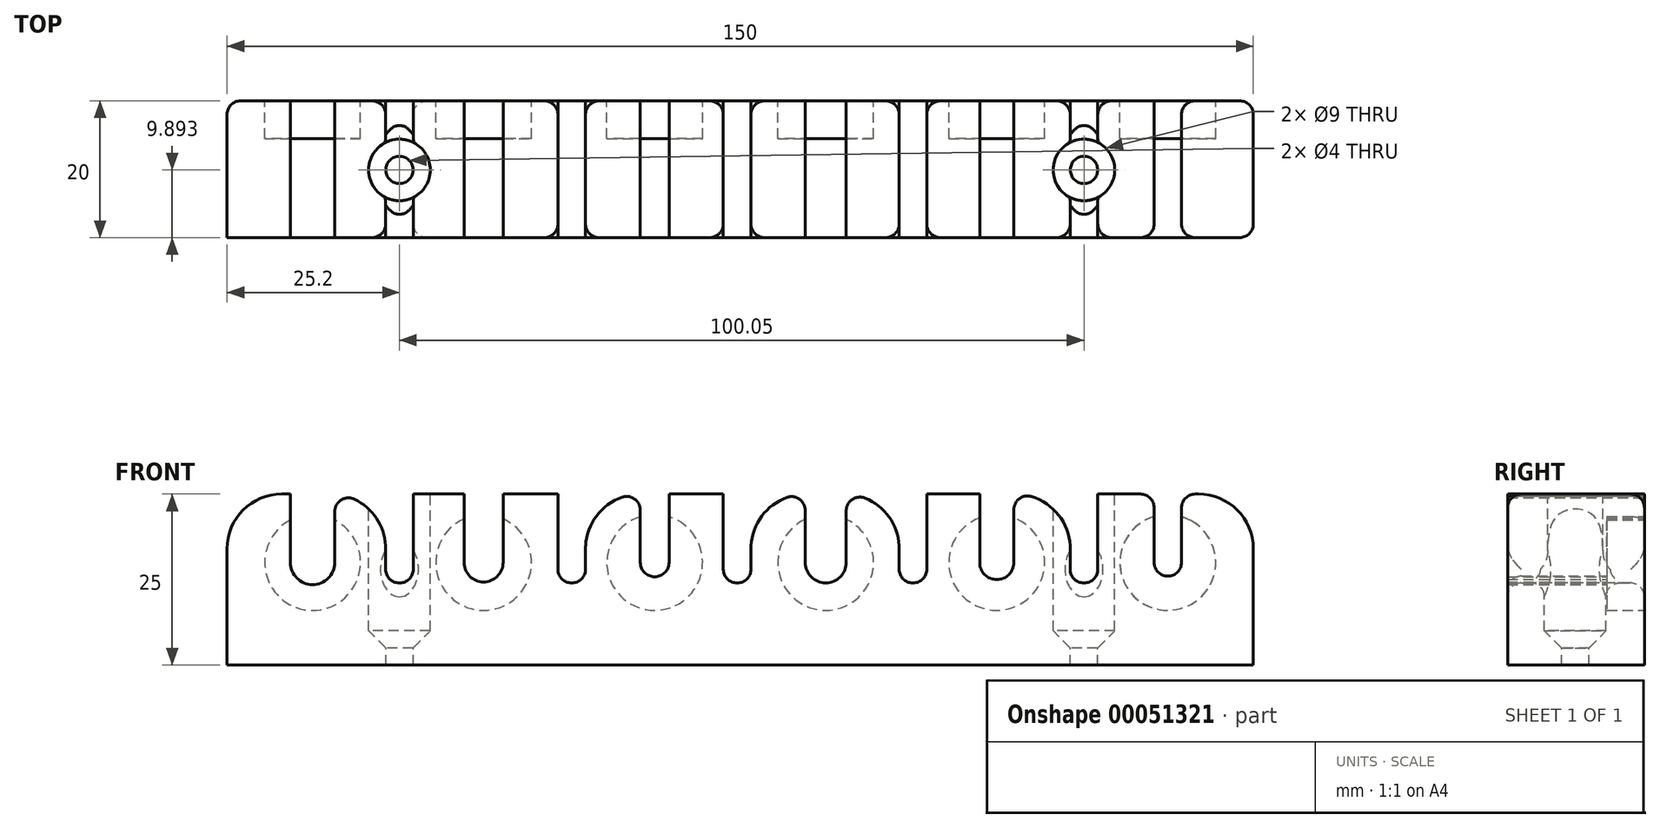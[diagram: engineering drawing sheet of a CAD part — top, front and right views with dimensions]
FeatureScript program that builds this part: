
annotation { "Feature Type Name" : "Feature", "Feature Type Description" : "" }
export const myFeature = defineFeature(function(context is Context, id is Id, definition is map)
    precondition{}
    {
        {
            var Q0;
            Q0=qCreatedBy(makeId("Top.planeOp"),FACE);
            var sketch = newSketch(context, id + "F0", { "sketchPlane" : qUnion([Q0])});
            skLineSegment(sketch, "E0.bottom", {"start": v(0, 0) * mm, "end": v(150, 0) * mm});
            skLineSegment(sketch, "E0.top", {"start": v(0, 20) * mm, "end": v(150, 20) * mm});
            skLineSegment(sketch, "E0.left", {"start": v(0, 0) * mm, "end": v(0, 20) * mm});
            skLineSegment(sketch, "E0.right", {"start": v(150, 0) * mm, "end": v(150, 20) * mm});
            skSolve(sketch);
        }
        {
            var Q0;
            Q0 = qSketchRegion(id + "F0", true);
            extrude(context, id + "F1", {"entities" : qUnion([Q0]), "depth" : 25 * mm});
        }
        {
            var Q0;
            Q0=makeQuery(id+"F1.opExtrude","SWEPT_FACE",FACE,{"disambiguationData":[OSD([sQuery(id+"F0.wireOp",EDGE,"E0.top")])]});
            var sketch = newSketch(context, id + "F2", { "sketchPlane" : qUnion([Q0])});
            skLineSegment(sketch, "E1", {"start": v(0, 15) * mm, "end": v(-150, 15) * mm, "construction": true});
            skLineSegment(sketch, "E2", {"start": v(-75, 0) * mm, "end": v(-75, 25) * mm, "construction": true});
            skCircle(sketch, "E3", {"center": v(-62.5, 15) * mm, "radius": 7 * mm});
            skCircle(sketch, "E4", {"center": v(-37.5, 15) * mm, "radius": 7 * mm});
            skCircle(sketch, "E5", {"center": v(-12.5, 15) * mm, "radius": 7 * mm});
            skCircle(sketch, "E6.MirrorC", {"center": v(-87.5, 15) * mm, "radius": 7 * mm});
            skCircle(sketch, "E7.MirrorC", {"center": v(-112.5, 15) * mm, "radius": 7 * mm});
            skCircle(sketch, "E8.MirrorC", {"center": v(-137.5, 15) * mm, "radius": 7 * mm});
            skSolve(sketch);
        }
        {
            var Q0;
            Q0 = qSketchRegion(id + "F2", true);
            extrude(context, id + "F3", {"entities" : qUnion([Q0]), "operationType" : NewBodyOperationType.REMOVE, "oppositeDirection" : true, "depth" : 5.5 * mm});
        }
        {
            var Q0;
            Q0=makeQuery(id+"F1.opExtrude","SWEPT_FACE",FACE,{"disambiguationData":[OSD([sQuery(id+"F0.wireOp",EDGE,"E0.top")])]});
            var sketch = newSketch(context, id + "F4", { "sketchPlane" : qUnion([Q0])});
            skCircle(sketch, "E9", {"center": v(-12.5, 15) * mm, "radius": 3.25 * mm});
            skCircle(sketch, "E10", {"center": v(-37.5, 15) * mm, "radius": 2.85 * mm});
            skCircle(sketch, "E11", {"center": v(-62.5, 15) * mm, "radius": 2.1 * mm});
            skCircle(sketch, "E12", {"center": v(-87.5, 15) * mm, "radius": 3 * mm});
            skCircle(sketch, "E13", {"center": v(-112.5, 15) * mm, "radius": 2.5 * mm});
            skCircle(sketch, "E14", {"center": v(-137.5, 15) * mm, "radius": 2 * mm});
            skSolve(sketch);
        }
        {
            var Q0;
            Q0 = qSketchRegion(id + "F4", true);
            extrude(context, id + "F5", {"entities" : qUnion([Q0]), "operationType" : NewBodyOperationType.REMOVE, "endBound" : BoundingType.THROUGH_ALL, "oppositeDirection" : true, "depth" : 25 * mm});
        }
        {
            var Q0;
            Q0=makeQuery(id+"F1.opExtrude","CAP_FACE",FACE,{"disambiguationData":[OSD([sQuery(id+"F0.wireOp",EDGE,"E0.bottom"),sQuery(id+"F0.wireOp",EDGE,"E0.top"),sQuery(id+"F0.wireOp",EDGE,"E0.left"),sQuery(id+"F0.wireOp",EDGE,"E0.right")])],"isStart":false});
            var sketch = newSketch(context, id + "F6", { "sketchPlane" : qUnion([Q0])});
            skLineSegment(sketch, "E15.0", {"start": v(135.5, 14.5) * mm, "end": v(139.5, 14.5) * mm});
            skLineSegment(sketch, "E16.0", {"start": v(110, 14.5) * mm, "end": v(115, 14.5) * mm});
            skLineSegment(sketch, "E17.0", {"start": v(84.5, 14.5) * mm, "end": v(90.5, 14.5) * mm});
            skLineSegment(sketch, "E18.0", {"start": v(60.4, 14.5) * mm, "end": v(64.6, 14.5) * mm});
            skLineSegment(sketch, "E19.0", {"start": v(34.65, 14.5) * mm, "end": v(40.35, 14.5) * mm});
            skLineSegment(sketch, "E20.0", {"start": v(9.25, 14.5) * mm, "end": v(15.75, 14.5) * mm});
            skLineSegment(sketch, "E21", {"start": v(9.25, 20) * mm, "end": v(9.25, 0) * mm});
            skLineSegment(sketch, "E22", {"start": v(9.25, 0) * mm, "end": v(15.75, 0) * mm});
            skLineSegment(sketch, "E23", {"start": v(15.75, 0) * mm, "end": v(15.75, 20) * mm});
            skLineSegment(sketch, "E24", {"start": v(15.75, 20) * mm, "end": v(9.25, 20) * mm});
            skLineSegment(sketch, "E25", {"start": v(34.65, 14.5) * mm, "end": v(34.65, 20) * mm});
            skLineSegment(sketch, "E26", {"start": v(34.65, 20) * mm, "end": v(40.35, 20) * mm});
            skLineSegment(sketch, "E27", {"start": v(40.35, 20) * mm, "end": v(40.35, 0) * mm});
            skLineSegment(sketch, "E28", {"start": v(40.35, 0) * mm, "end": v(34.65, 0) * mm});
            skLineSegment(sketch, "E29", {"start": v(34.65, 0) * mm, "end": v(34.65, 14.5) * mm});
            skLineSegment(sketch, "E30", {"start": v(60.4, 14.5) * mm, "end": v(60.4, 20) * mm});
            skLineSegment(sketch, "E31", {"start": v(60.4, 20) * mm, "end": v(64.6, 20) * mm});
            skLineSegment(sketch, "E32", {"start": v(64.6, 20) * mm, "end": v(64.6, 0) * mm});
            skLineSegment(sketch, "E33", {"start": v(64.6, 0) * mm, "end": v(60.4, 0) * mm});
            skLineSegment(sketch, "E34", {"start": v(60.4, 0) * mm, "end": v(60.4, 14.5) * mm});
            skLineSegment(sketch, "E35", {"start": v(84.5, 14.5) * mm, "end": v(84.5, 20) * mm});
            skLineSegment(sketch, "E36", {"start": v(84.5, 20) * mm, "end": v(90.5, 20) * mm});
            skLineSegment(sketch, "E37", {"start": v(90.5, 20) * mm, "end": v(90.5, 0) * mm});
            skLineSegment(sketch, "E38", {"start": v(90.5, 0) * mm, "end": v(84.5, 0) * mm});
            skLineSegment(sketch, "E39", {"start": v(84.5, 0) * mm, "end": v(84.5, 14.5) * mm});
            skLineSegment(sketch, "E40", {"start": v(110, 14.5) * mm, "end": v(110, 20) * mm});
            skLineSegment(sketch, "E41", {"start": v(110, 20) * mm, "end": v(115, 20) * mm});
            skLineSegment(sketch, "E42", {"start": v(115, 20) * mm, "end": v(115, 0) * mm});
            skLineSegment(sketch, "E43", {"start": v(115, 0) * mm, "end": v(110, 0) * mm});
            skLineSegment(sketch, "E44", {"start": v(110, 0) * mm, "end": v(110, 14.5) * mm});
            skLineSegment(sketch, "E45.bottom", {"start": v(135.5, 20) * mm, "end": v(139.5, 20) * mm});
            skLineSegment(sketch, "E45.top", {"start": v(135.5, 0) * mm, "end": v(139.5, 0) * mm});
            skLineSegment(sketch, "E45.left", {"start": v(135.5, 20) * mm, "end": v(135.5, 0) * mm});
            skLineSegment(sketch, "E45.right", {"start": v(139.5, 20) * mm, "end": v(139.5, 0) * mm});
            skSolve(sketch);
        }
        {
            var Q0;
            {var subQ0=sQuery(id+"F6.wireOp",EDGE,"E15.0");Q0=makeQuery(id+"F6.imprint","IMPRINT",FACE,{"disambiguationData":[TD([[makeQuery(id+"F6.imprint","IMPRINT",EDGE,{"derivedFrom":subQ0}),1.0]])]});}
            var Q1;
            {var subQ0=sQuery(id+"F6.wireOp",EDGE,"E15.0");Q1=makeQuery(id+"F6.imprint","IMPRINT",FACE,{"disambiguationData":[TD([[makeQuery(id+"F6.imprint","IMPRINT",EDGE,{"derivedFrom":subQ0}),-1.0]])]});}
            var Q2;
            {var subQ0=sQuery(id+"F6.wireOp",EDGE,"E16.0");Q2=makeQuery(id+"F6.imprint","IMPRINT",FACE,{"disambiguationData":[TD([[makeQuery(id+"F6.imprint","IMPRINT",EDGE,{"derivedFrom":subQ0}),1.0]])]});}
            var Q3;
            {var subQ0=sQuery(id+"F6.wireOp",EDGE,"E16.0");Q3=makeQuery(id+"F6.imprint","IMPRINT",FACE,{"disambiguationData":[TD([[makeQuery(id+"F6.imprint","IMPRINT",EDGE,{"derivedFrom":subQ0}),-1.0]])]});}
            var Q4;
            {var subQ0=sQuery(id+"F6.wireOp",EDGE,"E17.0");Q4=makeQuery(id+"F6.imprint","IMPRINT",FACE,{"disambiguationData":[TD([[makeQuery(id+"F6.imprint","IMPRINT",EDGE,{"derivedFrom":subQ0}),1.0]])]});}
            var Q5;
            {var subQ0=sQuery(id+"F6.wireOp",EDGE,"E17.0");Q5=makeQuery(id+"F6.imprint","IMPRINT",FACE,{"disambiguationData":[TD([[makeQuery(id+"F6.imprint","IMPRINT",EDGE,{"derivedFrom":subQ0}),-1.0]])]});}
            var Q6;
            {var subQ0=sQuery(id+"F6.wireOp",EDGE,"E18.0");Q6=makeQuery(id+"F6.imprint","IMPRINT",FACE,{"disambiguationData":[TD([[makeQuery(id+"F6.imprint","IMPRINT",EDGE,{"derivedFrom":subQ0}),1.0]])]});}
            var Q7;
            {var subQ0=sQuery(id+"F6.wireOp",EDGE,"E18.0");Q7=makeQuery(id+"F6.imprint","IMPRINT",FACE,{"disambiguationData":[TD([[makeQuery(id+"F6.imprint","IMPRINT",EDGE,{"derivedFrom":subQ0}),-1.0]])]});}
            var Q8;
            {var subQ0=sQuery(id+"F6.wireOp",EDGE,"E19.0");Q8=makeQuery(id+"F6.imprint","IMPRINT",FACE,{"disambiguationData":[TD([[makeQuery(id+"F6.imprint","IMPRINT",EDGE,{"derivedFrom":subQ0}),1.0]])]});}
            var Q9;
            {var subQ0=sQuery(id+"F6.wireOp",EDGE,"E19.0");Q9=makeQuery(id+"F6.imprint","IMPRINT",FACE,{"disambiguationData":[TD([[makeQuery(id+"F6.imprint","IMPRINT",EDGE,{"derivedFrom":subQ0}),-1.0]])]});}
            var Q10;
            {var subQ0=sQuery(id+"F6.wireOp",EDGE,"E20.0");Q10=makeQuery(id+"F6.imprint","IMPRINT",FACE,{"disambiguationData":[TD([[makeQuery(id+"F6.imprint","IMPRINT",EDGE,{"derivedFrom":subQ0}),1.0]])]});}
            var Q11;
            {var subQ0=sQuery(id+"F6.wireOp",EDGE,"E20.0");Q11=makeQuery(id+"F6.imprint","IMPRINT",FACE,{"disambiguationData":[TD([[makeQuery(id+"F6.imprint","IMPRINT",EDGE,{"derivedFrom":subQ0}),-1.0]])]});}
            extrude(context, id + "F7", {"entities" : qUnion([Q0, Q1, Q2, Q3, Q4, Q5, Q6, Q7, Q8, Q9, Q10, Q11]), "operationType" : NewBodyOperationType.REMOVE, "oppositeDirection" : true, "depth" : 10 * mm});
        }
        {
            var Q0;
            {var subQ0=sQuery(id+"F0.wireOp",EDGE,"E0.bottom");var subQ1=sQuery(id+"F0.wireOp",EDGE,"E0.top");Q0=makeQuery(id+"F7.boolean.opBoolean","SPLIT",FACE,{"disambiguationData":[TD([makeQuery(id+"F7.opExtrude","SWEPT_FACE",FACE,{"disambiguationData":[OSD([sQuery(id+"F6.wireOp",EDGE,"E42")])]})])],"derivedFrom":makeQuery(id+"F1.opExtrude","CAP_FACE",FACE,{"disambiguationData":[OSD([subQ0,subQ1,sQuery(id+"F0.wireOp",EDGE,"E0.left"),sQuery(id+"F0.wireOp",EDGE,"E0.right")])],"isStart":false})});}
            var sketch = newSketch(context, id + "F8", { "sketchPlane" : qUnion([Q0])});
            skLineSegment(sketch, "E46", {"start": v(0, 9.9) * mm, "end": v(150, 9.9) * mm, "construction": true});
            skCircle(sketch, "E47", {"center": v(25.2, 9.9) * mm, "radius": 2 * mm});
            skCircle(sketch, "E48", {"center": v(125.25, 9.9) * mm, "radius": 2 * mm});
            skLineSegment(sketch, "E49", {"start": v(25.2, 0) * mm, "end": v(25.2, 19.66) * mm, "construction": true});
            skLineSegment(sketch, "E50", {"start": v(125.25, 20) * mm, "end": v(125.25, 0) * mm, "construction": true});
            skSolve(sketch);
        }
        {
            var Q0;
            Q0 = qSketchRegion(id + "F8", true);
            extrude(context, id + "F9", {"entities" : qUnion([Q0]), "operationType" : NewBodyOperationType.REMOVE, "endBound" : BoundingType.THROUGH_ALL, "oppositeDirection" : true, "depth" : 20 * mm});
        }
        {
            var Q0;
            {var subQ0=sQuery(id+"F0.wireOp",EDGE,"E0.bottom");var subQ1=sQuery(id+"F0.wireOp",EDGE,"E0.top");Q0=makeQuery(id+"F7.boolean.opBoolean","SPLIT",FACE,{"disambiguationData":[TD([makeQuery(id+"F7.opExtrude","SWEPT_FACE",FACE,{"disambiguationData":[OSD([sQuery(id+"F6.wireOp",EDGE,"E23")])]})])],"derivedFrom":makeQuery(id+"F1.opExtrude","CAP_FACE",FACE,{"disambiguationData":[OSD([subQ0,subQ1,sQuery(id+"F0.wireOp",EDGE,"E0.left"),sQuery(id+"F0.wireOp",EDGE,"E0.right")])],"isStart":false})});}
            var sketch = newSketch(context, id + "F10", { "sketchPlane" : qUnion([Q0])});
            skCircle(sketch, "E51", {"center": v(25.2, 9.9) * mm, "radius": 4.5 * mm});
            skCircle(sketch, "E52", {"center": v(125.25, 9.9) * mm, "radius": 4.5 * mm});
            skSolve(sketch);
        }
        {
            var Q0;
            Q0 = qSketchRegion(id + "F10", true);
            extrude(context, id + "F11", {"entities" : qUnion([Q0]), "operationType" : NewBodyOperationType.REMOVE, "oppositeDirection" : true, "depth" : 20 * mm});
        }
        {
            var Q0;
            Q0=makeQuery(id+"F11.boolean.opBoolean","INTERSECT",EDGE,{"derivedFrom":[makeQuery(id+"F9.boolean.opBoolean","COPY",FACE,{"derivedFrom":makeQuery(id+"F9.opExtrude","SWEPT_FACE",FACE,{"disambiguationData":[OSD([sQuery(id+"F8.wireOp",EDGE,"E47")])]})}),makeQuery(id+"F11.opExtrude","CAP_FACE",FACE,{"disambiguationData":[OSD([sQuery(id+"F10.wireOp",EDGE,"E51")])],"isStart":false})]});
            var Q1;
            Q1=makeQuery(id+"F11.boolean.opBoolean","INTERSECT",EDGE,{"derivedFrom":[makeQuery(id+"F9.boolean.opBoolean","COPY",FACE,{"derivedFrom":makeQuery(id+"F9.opExtrude","SWEPT_FACE",FACE,{"disambiguationData":[OSD([sQuery(id+"F8.wireOp",EDGE,"E48")])]})}),makeQuery(id+"F11.opExtrude","CAP_FACE",FACE,{"disambiguationData":[OSD([sQuery(id+"F10.wireOp",EDGE,"E52")])],"isStart":false})]});
            chamfer(context, id + "F12", {"entities" : qUnion([Q0, Q1]), "width" : 2.5 * mm, "tangentPropagation" : true});
        }
        {
            var Q0;
            {var subQ0=sQuery(id+"F0.wireOp",EDGE,"E0.bottom");var subQ1=sQuery(id+"F0.wireOp",EDGE,"E0.top");Q0=makeQuery(id+"F7.boolean.opBoolean","SPLIT",FACE,{"disambiguationData":[TD([makeQuery(id+"F7.opExtrude","SWEPT_FACE",FACE,{"disambiguationData":[OSD([sQuery(id+"F6.wireOp",EDGE,"E27")])]})])],"derivedFrom":makeQuery(id+"F1.opExtrude","CAP_FACE",FACE,{"disambiguationData":[OSD([subQ0,subQ1,sQuery(id+"F0.wireOp",EDGE,"E0.left"),sQuery(id+"F0.wireOp",EDGE,"E0.right")])],"isStart":false})});}
            var sketch = newSketch(context, id + "F13", { "sketchPlane" : qUnion([Q0])});
            skLineSegment(sketch, "E53.bottom", {"start": v(48.36, 20) * mm, "end": v(52.4, 20) * mm});
            skLineSegment(sketch, "E53.top", {"start": v(48.36, 0) * mm, "end": v(52.4, 0) * mm});
            skLineSegment(sketch, "E53.left", {"start": v(48.36, 20) * mm, "end": v(48.36, 0) * mm});
            skLineSegment(sketch, "E53.right", {"start": v(52.4, 20) * mm, "end": v(52.4, 0) * mm});
            skLineSegment(sketch, "E54.bottom", {"start": v(72.53, 20) * mm, "end": v(76.57, 20) * mm});
            skLineSegment(sketch, "E54.top", {"start": v(72.53, 0) * mm, "end": v(76.57, 0) * mm});
            skLineSegment(sketch, "E54.left", {"start": v(72.53, 20) * mm, "end": v(72.53, 0) * mm});
            skLineSegment(sketch, "E54.right", {"start": v(76.57, 20) * mm, "end": v(76.57, 0) * mm});
            skLineSegment(sketch, "E55.bottom", {"start": v(98.23, 0) * mm, "end": v(102.27, 0) * mm});
            skLineSegment(sketch, "E55.top", {"start": v(98.23, 20) * mm, "end": v(102.27, 20) * mm});
            skLineSegment(sketch, "E55.left", {"start": v(98.23, 0) * mm, "end": v(98.23, 20) * mm});
            skLineSegment(sketch, "E55.right", {"start": v(102.27, 0) * mm, "end": v(102.27, 20) * mm});
            skLineSegment(sketch, "E56", {"start": v(50.38, 20) * mm, "end": v(50.38, 0) * mm, "construction": true});
            skLineSegment(sketch, "E57", {"start": v(74.55, 20) * mm, "end": v(74.55, 0) * mm, "construction": true});
            skLineSegment(sketch, "E58", {"start": v(100.25, 20) * mm, "end": v(100.25, 0) * mm, "construction": true});
            skLineSegment(sketch, "E59.bottom", {"start": v(23.18, 0) * mm, "end": v(27.22, 0) * mm});
            skLineSegment(sketch, "E59.top", {"start": v(23.18, 20) * mm, "end": v(27.22, 20) * mm});
            skLineSegment(sketch, "E59.left", {"start": v(23.18, 0) * mm, "end": v(23.18, 20) * mm});
            skLineSegment(sketch, "E59.right", {"start": v(27.22, 0) * mm, "end": v(27.22, 20) * mm});
            skLineSegment(sketch, "E60", {"start": v(25.2, 20) * mm, "end": v(25.2, 0) * mm, "construction": true});
            skLineSegment(sketch, "E61.bottom", {"start": v(123.23, 0) * mm, "end": v(127.27, 0) * mm});
            skLineSegment(sketch, "E61.top", {"start": v(123.23, 20) * mm, "end": v(127.27, 20) * mm});
            skLineSegment(sketch, "E61.left", {"start": v(123.23, 0) * mm, "end": v(123.23, 20) * mm});
            skLineSegment(sketch, "E61.right", {"start": v(127.27, 0) * mm, "end": v(127.27, 20) * mm});
            skLineSegment(sketch, "E62", {"start": v(125.25, 20) * mm, "end": v(125.25, 0) * mm, "construction": true});
            skSolve(sketch);
        }
        {
            var Q0;
            Q0 = qSketchRegion(id + "F13", true);
            extrude(context, id + "F14", {"entities" : qUnion([Q0]), "operationType" : NewBodyOperationType.REMOVE, "oppositeDirection" : true, "depth" : 13 * mm});
        }
        {
            var Q0;
            Q0=makeQuery(id+"F14.boolean.opBoolean","COPY",EDGE,{"derivedFrom":makeQuery(id+"F14.opExtrude","CAP_EDGE",EDGE,{"disambiguationData":[OSD([sQuery(id+"F13.wireOp",EDGE,"E53.left")])],"isStart":true})});
            var Q1;
            Q1=makeQuery(id+"F14.boolean.opBoolean","COPY",EDGE,{"derivedFrom":makeQuery(id+"F14.opExtrude","CAP_EDGE",EDGE,{"disambiguationData":[OSD([sQuery(id+"F13.wireOp",EDGE,"E53.right")])],"isStart":true})});
            var Q2;
            Q2=makeQuery(id+"F14.boolean.opBoolean","COPY",EDGE,{"derivedFrom":makeQuery(id+"F14.opExtrude","CAP_EDGE",EDGE,{"disambiguationData":[OSD([sQuery(id+"F13.wireOp",EDGE,"E54.left")])],"isStart":true})});
            var Q3;
            Q3=makeQuery(id+"F14.boolean.opBoolean","COPY",EDGE,{"derivedFrom":makeQuery(id+"F14.opExtrude","CAP_EDGE",EDGE,{"disambiguationData":[OSD([sQuery(id+"F13.wireOp",EDGE,"E54.right")])],"isStart":true})});
            var Q4;
            Q4=makeQuery(id+"F14.boolean.opBoolean","COPY",EDGE,{"derivedFrom":makeQuery(id+"F14.opExtrude","CAP_EDGE",EDGE,{"disambiguationData":[OSD([sQuery(id+"F13.wireOp",EDGE,"E55.left")])],"isStart":true})});
            var Q5;
            Q5=makeQuery(id+"F14.boolean.opBoolean","COPY",EDGE,{"derivedFrom":makeQuery(id+"F14.opExtrude","CAP_EDGE",EDGE,{"disambiguationData":[OSD([sQuery(id+"F13.wireOp",EDGE,"E55.right")])],"isStart":true})});
            var Q6;
            Q6=makeQuery(id+"F1.opExtrude","CAP_EDGE",EDGE,{"disambiguationData":[OSD([sQuery(id+"F0.wireOp",EDGE,"E0.right")])],"isStart":false});
            var Q7;
            Q7=makeQuery(id+"F1.opExtrude","CAP_EDGE",EDGE,{"disambiguationData":[OSD([sQuery(id+"F0.wireOp",EDGE,"E0.left")])],"isStart":false});
            var Q8;
            {var subQ0=sQuery(id+"F0.wireOp",EDGE,"E0.top");var subQ1=sQuery(id+"F0.wireOp",EDGE,"E0.bottom");var subQ3=sQuery(id+"F13.wireOp",EDGE,"E59.left");var subQ6=makeQuery(id+"F14.opExtrude","CAP_EDGE",EDGE,{"disambiguationData":[OSD([subQ3])],"isStart":true});Q8=qUnion([makeQuery(id+"F14.boolean.opBoolean","COPY",EDGE,{"disambiguationData":[TD([makeQuery(id+"F1.opExtrude","SWEPT_FACE",FACE,{"disambiguationData":[OSD([subQ1])]})])],"derivedFrom":subQ6}),makeQuery(id+"F14.boolean.opBoolean","COPY",EDGE,{"disambiguationData":[TD([makeQuery(id+"F1.opExtrude","SWEPT_FACE",FACE,{"disambiguationData":[OSD([subQ0])]})])],"derivedFrom":subQ6})]);}
            var Q9;
            {var subQ0=sQuery(id+"F0.wireOp",EDGE,"E0.top");var subQ1=sQuery(id+"F0.wireOp",EDGE,"E0.bottom");var subQ4=sQuery(id+"F13.wireOp",EDGE,"E59.right");var subQ6=makeQuery(id+"F14.opExtrude","CAP_EDGE",EDGE,{"disambiguationData":[OSD([subQ4])],"isStart":true});Q9=qUnion([makeQuery(id+"F14.boolean.opBoolean","COPY",EDGE,{"disambiguationData":[TD([makeQuery(id+"F1.opExtrude","SWEPT_FACE",FACE,{"disambiguationData":[OSD([subQ1])]})])],"derivedFrom":subQ6}),makeQuery(id+"F14.boolean.opBoolean","COPY",EDGE,{"disambiguationData":[TD([makeQuery(id+"F1.opExtrude","SWEPT_FACE",FACE,{"disambiguationData":[OSD([subQ0])]})])],"derivedFrom":subQ6})]);}
            var Q10;
            {var subQ0=sQuery(id+"F0.wireOp",EDGE,"E0.top");var subQ1=sQuery(id+"F0.wireOp",EDGE,"E0.bottom");var subQ4=sQuery(id+"F13.wireOp",EDGE,"E61.left");var subQ6=makeQuery(id+"F14.opExtrude","CAP_EDGE",EDGE,{"disambiguationData":[OSD([subQ4])],"isStart":true});Q10=qUnion([makeQuery(id+"F14.boolean.opBoolean","COPY",EDGE,{"disambiguationData":[TD([makeQuery(id+"F1.opExtrude","SWEPT_FACE",FACE,{"disambiguationData":[OSD([subQ1])]})])],"derivedFrom":subQ6}),makeQuery(id+"F14.boolean.opBoolean","COPY",EDGE,{"disambiguationData":[TD([makeQuery(id+"F1.opExtrude","SWEPT_FACE",FACE,{"disambiguationData":[OSD([subQ0])]})])],"derivedFrom":subQ6})]);}
            var Q11;
            {var subQ0=sQuery(id+"F0.wireOp",EDGE,"E0.top");var subQ1=sQuery(id+"F0.wireOp",EDGE,"E0.bottom");var subQ4=sQuery(id+"F13.wireOp",EDGE,"E61.right");var subQ6=makeQuery(id+"F14.opExtrude","CAP_EDGE",EDGE,{"disambiguationData":[OSD([subQ4])],"isStart":true});Q11=qUnion([makeQuery(id+"F14.boolean.opBoolean","COPY",EDGE,{"disambiguationData":[TD([makeQuery(id+"F1.opExtrude","SWEPT_FACE",FACE,{"disambiguationData":[OSD([subQ1])]})])],"derivedFrom":subQ6}),makeQuery(id+"F14.boolean.opBoolean","COPY",EDGE,{"disambiguationData":[TD([makeQuery(id+"F1.opExtrude","SWEPT_FACE",FACE,{"disambiguationData":[OSD([subQ0])]})])],"derivedFrom":subQ6})]);}
            fillet(context, id + "F15", {"entities" : qUnion([Q0, Q1, Q2, Q3, Q4, Q5, Q6, Q7, Q8, Q9, Q10, Q11]), "radius" : 8 * mm, "tangentPropagation" : true, "allowEdgeOverflow" : false});
        }
        {
            var Q0;
            Q0=makeQuery(id+"F7.boolean.opBoolean","COPY",EDGE,{"derivedFrom":makeQuery(id+"F7.opExtrude","CAP_EDGE",EDGE,{"disambiguationData":[OSD([sQuery(id+"F6.wireOp",EDGE,"E21")])],"isStart":true})});
            var Q1;
            {var subQ0=sQuery(id+"F0.wireOp",EDGE,"E0.bottom");var subQ1=sQuery(id+"F13.wireOp",EDGE,"E59.left");Q1=makeQuery(id+"F15.opFillet","BLEND_EDGE",EDGE,{"blendedFrom":[makeQuery(id+"F14.boolean.opBoolean","COPY",EDGE,{"disambiguationData":[TD([makeQuery(id+"F1.opExtrude","SWEPT_FACE",FACE,{"disambiguationData":[OSD([subQ0])]})])],"derivedFrom":makeQuery(id+"F14.opExtrude","CAP_EDGE",EDGE,{"disambiguationData":[OSD([subQ1])],"isStart":true})}),makeQuery(id+"F7.boolean.opBoolean","COPY",FACE,{"derivedFrom":makeQuery(id+"F7.opExtrude","SWEPT_FACE",FACE,{"disambiguationData":[OSD([sQuery(id+"F6.wireOp",EDGE,"E23")])]})})],"blendedInto":[makeQuery(id+"F7.boolean.opBoolean","COPY",FACE,{"derivedFrom":makeQuery(id+"F7.opExtrude","SWEPT_FACE",FACE,{"disambiguationData":[OSD([sQuery(id+"F6.wireOp",EDGE,"E23")])]})})]});}
            var Q2;
            {var subQ0=sQuery(id+"F0.wireOp",EDGE,"E0.bottom");var subQ1=sQuery(id+"F13.wireOp",EDGE,"E59.right");Q2=makeQuery(id+"F15.opFillet","BLEND_EDGE",EDGE,{"blendedFrom":[makeQuery(id+"F14.boolean.opBoolean","COPY",EDGE,{"disambiguationData":[TD([makeQuery(id+"F1.opExtrude","SWEPT_FACE",FACE,{"disambiguationData":[OSD([subQ0])]})])],"derivedFrom":makeQuery(id+"F14.opExtrude","CAP_EDGE",EDGE,{"disambiguationData":[OSD([subQ1])],"isStart":true})}),makeQuery(id+"F7.boolean.opBoolean","COPY",FACE,{"derivedFrom":makeQuery(id+"F7.opExtrude","SWEPT_FACE",FACE,{"disambiguationData":[OSD([sQuery(id+"F6.wireOp",EDGE,"E25"),sQuery(id+"F6.wireOp",EDGE,"E29")])]})})],"blendedInto":[makeQuery(id+"F7.boolean.opBoolean","COPY",FACE,{"derivedFrom":makeQuery(id+"F7.opExtrude","SWEPT_FACE",FACE,{"disambiguationData":[OSD([sQuery(id+"F6.wireOp",EDGE,"E25"),sQuery(id+"F6.wireOp",EDGE,"E29")])]})})]});}
            var Q3;
            Q3=makeQuery(id+"F15.opFillet","BLEND_EDGE",EDGE,{"blendedFrom":[makeQuery(id+"F14.boolean.opBoolean","COPY",EDGE,{"derivedFrom":makeQuery(id+"F14.opExtrude","CAP_EDGE",EDGE,{"disambiguationData":[OSD([sQuery(id+"F13.wireOp",EDGE,"E54.left")])],"isStart":true})}),makeQuery(id+"F7.boolean.opBoolean","COPY",FACE,{"derivedFrom":makeQuery(id+"F7.opExtrude","SWEPT_FACE",FACE,{"disambiguationData":[OSD([sQuery(id+"F6.wireOp",EDGE,"E32")])]})})],"blendedInto":[makeQuery(id+"F7.boolean.opBoolean","COPY",FACE,{"derivedFrom":makeQuery(id+"F7.opExtrude","SWEPT_FACE",FACE,{"disambiguationData":[OSD([sQuery(id+"F6.wireOp",EDGE,"E32")])]})})]});
            var Q4;
            Q4=makeQuery(id+"F7.boolean.opBoolean","COPY",EDGE,{"derivedFrom":makeQuery(id+"F7.opExtrude","CAP_EDGE",EDGE,{"disambiguationData":[OSD([sQuery(id+"F6.wireOp",EDGE,"E30"),sQuery(id+"F6.wireOp",EDGE,"E34")])],"isStart":true})});
            var Q5;
            Q5=makeQuery(id+"F15.opFillet","BLEND_EDGE",EDGE,{"blendedFrom":[makeQuery(id+"F14.boolean.opBoolean","COPY",EDGE,{"derivedFrom":makeQuery(id+"F14.opExtrude","CAP_EDGE",EDGE,{"disambiguationData":[OSD([sQuery(id+"F13.wireOp",EDGE,"E54.right")])],"isStart":true})}),makeQuery(id+"F7.boolean.opBoolean","COPY",FACE,{"derivedFrom":makeQuery(id+"F7.opExtrude","SWEPT_FACE",FACE,{"disambiguationData":[OSD([sQuery(id+"F6.wireOp",EDGE,"E35"),sQuery(id+"F6.wireOp",EDGE,"E39")])]})})],"blendedInto":[makeQuery(id+"F7.boolean.opBoolean","COPY",FACE,{"derivedFrom":makeQuery(id+"F7.opExtrude","SWEPT_FACE",FACE,{"disambiguationData":[OSD([sQuery(id+"F6.wireOp",EDGE,"E35"),sQuery(id+"F6.wireOp",EDGE,"E39")])]})})]});
            var Q6;
            Q6=makeQuery(id+"F15.opFillet","BLEND_EDGE",EDGE,{"blendedFrom":[makeQuery(id+"F14.boolean.opBoolean","COPY",EDGE,{"derivedFrom":makeQuery(id+"F14.opExtrude","CAP_EDGE",EDGE,{"disambiguationData":[OSD([sQuery(id+"F13.wireOp",EDGE,"E55.left")])],"isStart":true})}),makeQuery(id+"F7.boolean.opBoolean","COPY",FACE,{"derivedFrom":makeQuery(id+"F7.opExtrude","SWEPT_FACE",FACE,{"disambiguationData":[OSD([sQuery(id+"F6.wireOp",EDGE,"E37")])]})})],"blendedInto":[makeQuery(id+"F7.boolean.opBoolean","COPY",FACE,{"derivedFrom":makeQuery(id+"F7.opExtrude","SWEPT_FACE",FACE,{"disambiguationData":[OSD([sQuery(id+"F6.wireOp",EDGE,"E37")])]})})]});
            var Q7;
            Q7=makeQuery(id+"F15.opFillet","BLEND_EDGE",EDGE,{"blendedFrom":[makeQuery(id+"F14.boolean.opBoolean","COPY",EDGE,{"derivedFrom":makeQuery(id+"F14.opExtrude","CAP_EDGE",EDGE,{"disambiguationData":[OSD([sQuery(id+"F13.wireOp",EDGE,"E55.right")])],"isStart":true})}),makeQuery(id+"F7.boolean.opBoolean","COPY",FACE,{"derivedFrom":makeQuery(id+"F7.opExtrude","SWEPT_FACE",FACE,{"disambiguationData":[OSD([sQuery(id+"F6.wireOp",EDGE,"E40"),sQuery(id+"F6.wireOp",EDGE,"E44")])]})})],"blendedInto":[makeQuery(id+"F7.boolean.opBoolean","COPY",FACE,{"derivedFrom":makeQuery(id+"F7.opExtrude","SWEPT_FACE",FACE,{"disambiguationData":[OSD([sQuery(id+"F6.wireOp",EDGE,"E40"),sQuery(id+"F6.wireOp",EDGE,"E44")])]})})]});
            var Q8;
            Q8=makeQuery(id+"F7.boolean.opBoolean","COPY",EDGE,{"derivedFrom":makeQuery(id+"F7.opExtrude","CAP_EDGE",EDGE,{"disambiguationData":[OSD([sQuery(id+"F6.wireOp",EDGE,"E42")])],"isStart":true})});
            var Q9;
            {var subQ0=makeQuery(id+"F7.opExtrude","SWEPT_FACE",FACE,{"disambiguationData":[OSD([sQuery(id+"F6.wireOp",EDGE,"E45.left")])]});var subQ2=sQuery(id+"F0.wireOp",EDGE,"E0.top");var subQ4=sQuery(id+"F0.wireOp",EDGE,"E0.bottom");var subQ5=makeQuery(id+"F1.opExtrude","SWEPT_FACE",FACE,{"disambiguationData":[OSD([subQ4])]});var subQ6=sQuery(id+"F13.wireOp",EDGE,"E61.right");var subQ8=makeQuery(id+"F1.opExtrude","CAP_FACE",FACE,{"disambiguationData":[OSD([subQ4,subQ2,sQuery(id+"F0.wireOp",EDGE,"E0.left"),sQuery(id+"F0.wireOp",EDGE,"E0.right")])],"isStart":false});Q9=makeQuery(id+"F15.opFillet","BLEND_EDGE",EDGE,{"blendedFrom":[makeQuery(id+"F14.boolean.opBoolean","COPY",EDGE,{"disambiguationData":[TD([subQ5])],"derivedFrom":makeQuery(id+"F14.opExtrude","CAP_EDGE",EDGE,{"disambiguationData":[OSD([subQ6])],"isStart":true})}),makeQuery(id+"F14.boolean.opBoolean","SPLIT",FACE,{"disambiguationData":[TD([makeQuery(id+"F7.boolean.opBoolean","COPY",FACE,{"derivedFrom":subQ0})])],"derivedFrom":makeQuery(id+"F7.boolean.opBoolean","SPLIT",FACE,{"disambiguationData":[TD([makeQuery(id+"F7.opExtrude","SWEPT_FACE",FACE,{"disambiguationData":[OSD([sQuery(id+"F6.wireOp",EDGE,"E42")])]})])],"derivedFrom":subQ8})})],"blendedInto":[makeQuery(id+"F14.boolean.opBoolean","SPLIT",FACE,{"disambiguationData":[TD([makeQuery(id+"F7.boolean.opBoolean","COPY",FACE,{"derivedFrom":subQ0})])],"derivedFrom":makeQuery(id+"F7.boolean.opBoolean","SPLIT",FACE,{"disambiguationData":[TD([makeQuery(id+"F7.opExtrude","SWEPT_FACE",FACE,{"disambiguationData":[OSD([sQuery(id+"F6.wireOp",EDGE,"E42")])]})])],"derivedFrom":subQ8})})]});}
            var Q10;
            Q10=makeQuery(id+"F7.boolean.opBoolean","COPY",EDGE,{"derivedFrom":makeQuery(id+"F7.opExtrude","CAP_EDGE",EDGE,{"disambiguationData":[OSD([sQuery(id+"F6.wireOp",EDGE,"E45.left")])],"isStart":true})});
            var Q11;
            Q11=makeQuery(id+"F7.boolean.opBoolean","COPY",EDGE,{"derivedFrom":makeQuery(id+"F7.opExtrude","CAP_EDGE",EDGE,{"disambiguationData":[OSD([sQuery(id+"F6.wireOp",EDGE,"E45.right")])],"isStart":true})});
            fillet(context, id + "F16", {"entities" : qUnion([Q0, Q1, Q2, Q3, Q4, Q5, Q6, Q7, Q8, Q9, Q10, Q11]), "radius" : 2 * mm, "tangentPropagation" : true, "allowEdgeOverflow" : false});
        }
        {
            var Q0;
            {var subQ0=sQuery(id+"F13.wireOp",EDGE,"E59.left");var subQ1=sQuery(id+"F13.wireOp",EDGE,"E59.right");Q0=makeQuery(id+"F14.boolean.opBoolean","COPY",FACE,{"disambiguationData":[TD([makeQuery(id+"F1.opExtrude","SWEPT_FACE",FACE,{"disambiguationData":[OSD([sQuery(id+"F0.wireOp",EDGE,"E0.top")])]})])],"derivedFrom":makeQuery(id+"F14.opExtrude","CAP_FACE",FACE,{"disambiguationData":[OSD([sQuery(id+"F13.wireOp",EDGE,"E59.bottom"),sQuery(id+"F13.wireOp",EDGE,"E59.top"),subQ0,subQ1])],"isStart":false})});}
            var Q1;
            Q1=makeQuery(id+"F14.boolean.opBoolean","COPY",FACE,{"derivedFrom":makeQuery(id+"F14.opExtrude","CAP_FACE",FACE,{"disambiguationData":[OSD([sQuery(id+"F13.wireOp",EDGE,"E53.bottom"),sQuery(id+"F13.wireOp",EDGE,"E53.top"),sQuery(id+"F13.wireOp",EDGE,"E53.left"),sQuery(id+"F13.wireOp",EDGE,"E53.right")])],"isStart":false})});
            var Q2;
            Q2=makeQuery(id+"F14.boolean.opBoolean","COPY",FACE,{"derivedFrom":makeQuery(id+"F14.opExtrude","CAP_FACE",FACE,{"disambiguationData":[OSD([sQuery(id+"F13.wireOp",EDGE,"E54.bottom"),sQuery(id+"F13.wireOp",EDGE,"E54.top"),sQuery(id+"F13.wireOp",EDGE,"E54.left"),sQuery(id+"F13.wireOp",EDGE,"E54.right")])],"isStart":false})});
            var Q3;
            Q3=makeQuery(id+"F14.boolean.opBoolean","COPY",FACE,{"derivedFrom":makeQuery(id+"F14.opExtrude","CAP_FACE",FACE,{"disambiguationData":[OSD([sQuery(id+"F13.wireOp",EDGE,"E55.bottom"),sQuery(id+"F13.wireOp",EDGE,"E55.top"),sQuery(id+"F13.wireOp",EDGE,"E55.left"),sQuery(id+"F13.wireOp",EDGE,"E55.right")])],"isStart":false})});
            var Q4;
            {var subQ0=sQuery(id+"F13.wireOp",EDGE,"E61.left");var subQ1=sQuery(id+"F13.wireOp",EDGE,"E61.right");Q4=makeQuery(id+"F14.boolean.opBoolean","COPY",FACE,{"disambiguationData":[TD([makeQuery(id+"F1.opExtrude","SWEPT_FACE",FACE,{"disambiguationData":[OSD([sQuery(id+"F0.wireOp",EDGE,"E0.top")])]})])],"derivedFrom":makeQuery(id+"F14.opExtrude","CAP_FACE",FACE,{"disambiguationData":[OSD([sQuery(id+"F13.wireOp",EDGE,"E61.bottom"),sQuery(id+"F13.wireOp",EDGE,"E61.top"),subQ0,subQ1])],"isStart":false})});}
            fillet(context, id + "F17", {"entities" : qUnion([Q0, Q1, Q2, Q3, Q4]), "radius" : 2 * mm, "tangentPropagation" : true, "allowEdgeOverflow" : false});
        }
        {
            var Q0;
            {var subQ0=sQuery(id+"F13.wireOp",EDGE,"E59.left");var subQ1=sQuery(id+"F13.wireOp",EDGE,"E59.right");Q0=makeQuery(id+"F14.boolean.opBoolean","COPY",FACE,{"disambiguationData":[TD([makeQuery(id+"F1.opExtrude","SWEPT_FACE",FACE,{"disambiguationData":[OSD([sQuery(id+"F0.wireOp",EDGE,"E0.bottom")])]})])],"derivedFrom":makeQuery(id+"F14.opExtrude","CAP_FACE",FACE,{"disambiguationData":[OSD([sQuery(id+"F13.wireOp",EDGE,"E59.bottom"),sQuery(id+"F13.wireOp",EDGE,"E59.top"),subQ0,subQ1])],"isStart":false})});}
            var Q1;
            {var subQ0=sQuery(id+"F13.wireOp",EDGE,"E61.right");var subQ1=sQuery(id+"F13.wireOp",EDGE,"E61.left");Q1=makeQuery(id+"F14.boolean.opBoolean","COPY",FACE,{"disambiguationData":[TD([makeQuery(id+"F1.opExtrude","SWEPT_FACE",FACE,{"disambiguationData":[OSD([sQuery(id+"F0.wireOp",EDGE,"E0.bottom")])]})])],"derivedFrom":makeQuery(id+"F14.opExtrude","CAP_FACE",FACE,{"disambiguationData":[OSD([sQuery(id+"F13.wireOp",EDGE,"E61.bottom"),sQuery(id+"F13.wireOp",EDGE,"E61.top"),subQ1,subQ0])],"isStart":false})});}
            var Q2;
            Q2=makeQuery(id+"F15.opFillet","BLEND_EDGE",EDGE,{"blendedFrom":[makeQuery(id+"F1.opExtrude","CAP_EDGE",EDGE,{"disambiguationData":[OSD([sQuery(id+"F0.wireOp",EDGE,"E0.right")])],"isStart":false}),makeQuery(id+"F1.opExtrude","SWEPT_FACE",FACE,{"disambiguationData":[OSD([sQuery(id+"F0.wireOp",EDGE,"E0.bottom")])]})],"blendedInto":[makeQuery(id+"F1.opExtrude","SWEPT_FACE",FACE,{"disambiguationData":[OSD([sQuery(id+"F0.wireOp",EDGE,"E0.bottom")])]})]});
            var Q3;
            Q3=makeQuery(id+"F15.opFillet","BLEND_EDGE",EDGE,{"blendedFrom":[makeQuery(id+"F1.opExtrude","CAP_EDGE",EDGE,{"disambiguationData":[OSD([sQuery(id+"F0.wireOp",EDGE,"E0.right")])],"isStart":false}),makeQuery(id+"F1.opExtrude","SWEPT_FACE",FACE,{"disambiguationData":[OSD([sQuery(id+"F0.wireOp",EDGE,"E0.top")])]})],"blendedInto":[makeQuery(id+"F1.opExtrude","SWEPT_FACE",FACE,{"disambiguationData":[OSD([sQuery(id+"F0.wireOp",EDGE,"E0.top")])]})]});
            var Q4;
            Q4=makeQuery(id+"F15.opFillet","BLEND_EDGE",EDGE,{"blendedFrom":[makeQuery(id+"F1.opExtrude","CAP_EDGE",EDGE,{"disambiguationData":[OSD([sQuery(id+"F0.wireOp",EDGE,"E0.left")])],"isStart":false}),makeQuery(id+"F1.opExtrude","SWEPT_FACE",FACE,{"disambiguationData":[OSD([sQuery(id+"F0.wireOp",EDGE,"E0.top")])]})],"blendedInto":[makeQuery(id+"F1.opExtrude","SWEPT_FACE",FACE,{"disambiguationData":[OSD([sQuery(id+"F0.wireOp",EDGE,"E0.top")])]})]});
            fillet(context, id + "F18", {"entities" : qUnion([Q0, Q1, Q2, Q3, Q4]), "radius" : 2 * mm, "tangentPropagation" : true, "allowEdgeOverflow" : false});
        }
    });
